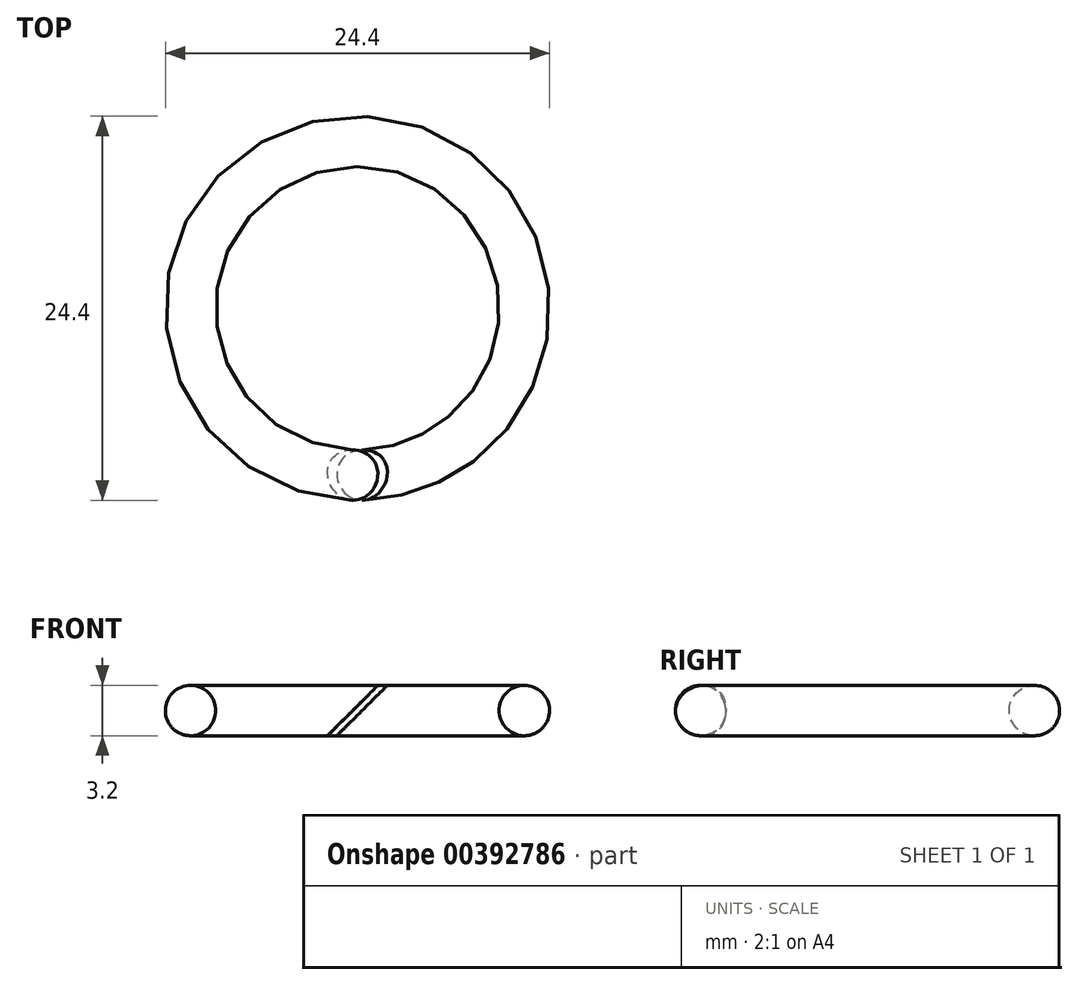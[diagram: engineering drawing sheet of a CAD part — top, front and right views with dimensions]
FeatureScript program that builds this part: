
annotation { "Feature Type Name" : "Feature", "Feature Type Description" : "" }
export const myFeature = defineFeature(function(context is Context, id is Id, definition is map)
    precondition{}
    {
        {
            assignVariable(context, id + "F0", {"name" : "ring_id", "anyValue" : 18});
        }
        {
            assignVariable(context, id + "F1", {"name" : "tube_diam", "anyValue" : 3.2});
        }
        {
            var Q0;
            Q0=qCreatedBy(makeId("Front.planeOp"),FACE);
            var sketch = newSketch(context, id + "F2", { "sketchPlane" : qUnion([Q0])});
            skCircle(sketch, "E0", {"center": v(10.6, 0) * mm, "radius": 1.6 * mm});
            skLineSegment(sketch, "E1", {"start": v(0, -4.73) * mm, "end": v(0, 9.22) * mm, "construction": true});
            skSolve(sketch);
        }
        {
            var Q0;
            Q0 = qSketchRegion(id + "F2", true);
            var Q1;
            Q1=sQuery(id+"F2.wireOp",EDGE,"E1");
            revolve(context, id + "F3", {"entities" : qUnion([Q0]), "axis" : qUnion([Q1]), "revolveType" : RevolveType.FULL});
        }
        {
            var Q0;
            Q0=qCreatedBy(makeId("Front.planeOp"),FACE);
            var sketch = newSketch(context, id + "F4", { "sketchPlane" : qUnion([Q0])});
            skLineSegment(sketch, "E2", {"start": v(9.8, 1.6) * mm, "end": v(-9.8, 1.6) * mm, "construction": true});
            skLineSegment(sketch, "E3", {"start": v(9.8, -1.6) * mm, "end": v(-9.8, -1.6) * mm, "construction": true});
            skLineSegment(sketch, "E4", {"start": v(-1.9, 1.6) * mm, "end": v(-1.9, -1.6) * mm, "construction": true});
            skLineSegment(sketch, "E5", {"start": v(-1.9, -1.6) * mm, "end": v(1.3, 1.6) * mm});
            skLineSegment(sketch, "E6", {"start": v(1.9, 1.6) * mm, "end": v(-1.3, -1.6) * mm});
            skLineSegment(sketch, "E7", {"start": v(-1.9, -1.6) * mm, "end": v(-1.3, -1.6) * mm});
            skLineSegment(sketch, "E8", {"start": v(1.3, 1.6) * mm, "end": v(1.9, 1.6) * mm});
            skLineSegment(sketch, "E9", {"start": v(-0.3, 0) * mm, "end": v(0.3, 0) * mm});
            skSolve(sketch);
        }
        {
            var Q0;
            Q0 = qSketchRegion(id + "F4", true);
            var Q1;
            Q1=makeQuery(id+"F3.opRevolve","SWEPT_BODY",BODY,{"disambiguationData":[OSD([sQuery(id+"F2.wireOp",EDGE,"E0")])]});
            extrude(context, id + "F5", {"entities" : qUnion([Q0]), "operationType" : NewBodyOperationType.REMOVE, "endBound" : BoundingType.THROUGH_ALL, "endBoundEntityBody" : qUnion([Q1]), "depth" : (getVariable(context, 'ring_id') + getVariable(context, 'tube_diam')) * mm});
        }
    });
